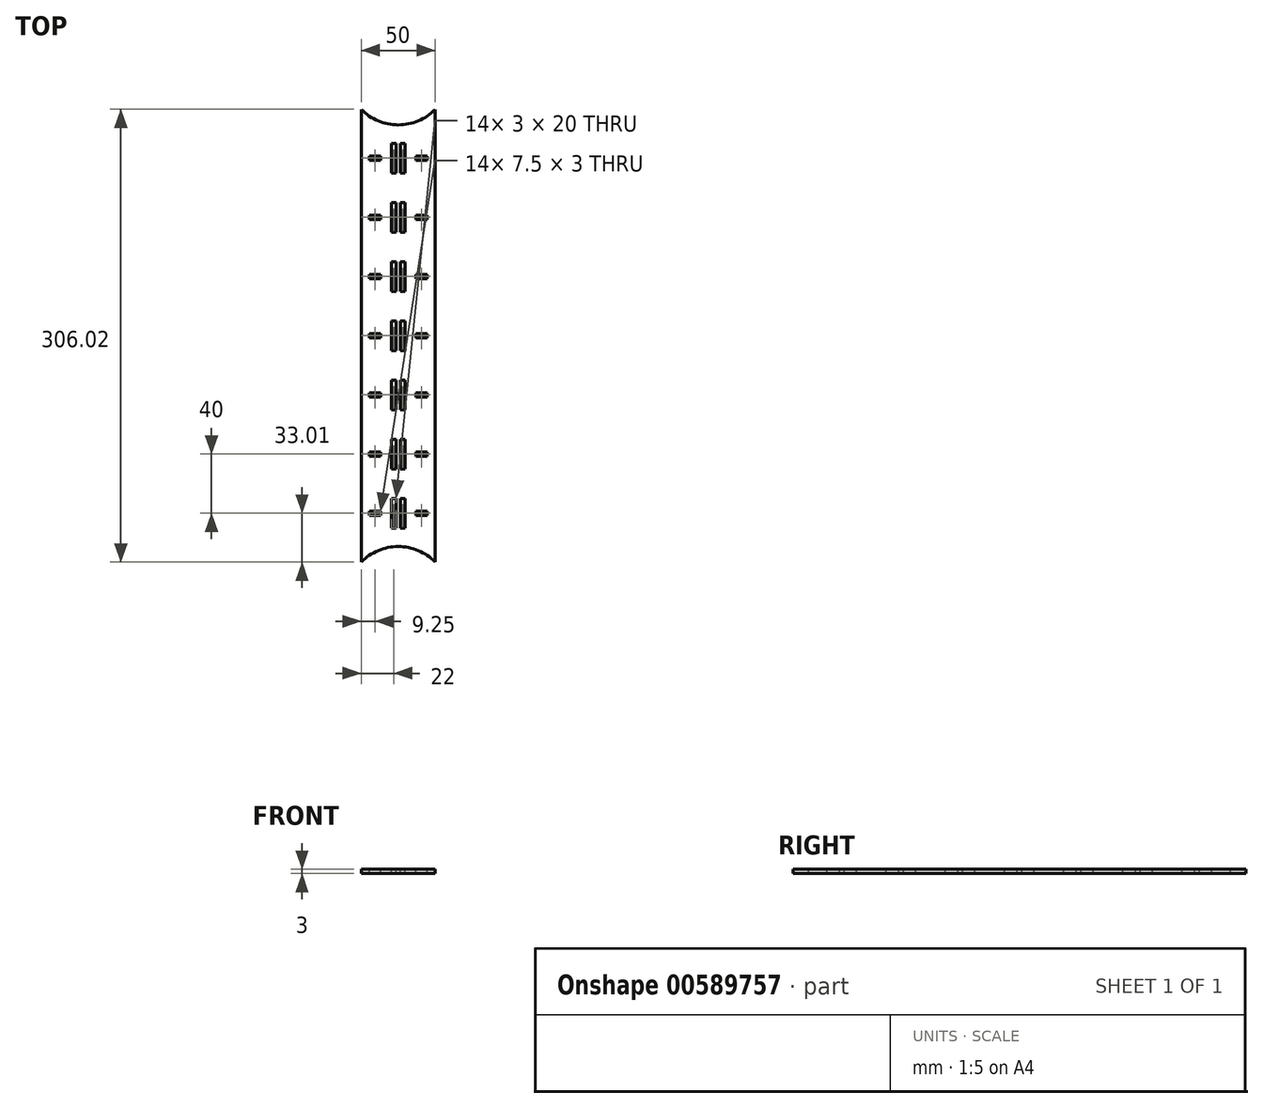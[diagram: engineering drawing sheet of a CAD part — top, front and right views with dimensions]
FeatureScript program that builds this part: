
annotation { "Feature Type Name" : "Feature", "Feature Type Description" : "" }
export const myFeature = defineFeature(function(context is Context, id is Id, definition is map)
    precondition{}
    {
        {
            var Q0;
            Q0=qCreatedBy(makeId("Top.planeOp"),FACE);
            var sketch = newSketch(context, id + "F0", { "sketchPlane" : qUnion([Q0])});
            skLineSegment(sketch, "E0.bottom", {"start": v(25, 140) * mm, "end": v(-25, 140) * mm});
            skLineSegment(sketch, "E0.top", {"start": v(25, -140) * mm, "end": v(-25, -140) * mm});
            skLineSegment(sketch, "E0.left", {"start": v(25, 140) * mm, "end": v(25, -140) * mm});
            skLineSegment(sketch, "E0.right", {"start": v(-25, 140) * mm, "end": v(-25, -140) * mm});
            skPoint(sketch, "E0.middle", {"position": v(0, 0) * mm});
            skSolve(sketch);
        }
        {
            var Q0;
            Q0=makeQuery(id+"F0.imprint","IMPRINT",FACE,{"disambiguationData":[TD([[makeQuery(id+"F0.imprint","IMPRINT",EDGE,{"derivedFrom":sQuery(id+"F0.wireOp",EDGE,"E0.bottom")}),1.0]])]});
            extrude(context, id + "F1", {"entities" : qUnion([Q0]), "depth" : 3 * mm, "offsetDistance" : 25 * mm});
        }
        {
            var Q0;
            Q0=makeQuery(id+"F1.opExtrude","CAP_FACE",FACE,{"disambiguationData":[OSD([sQuery(id+"F0.wireOp",EDGE,"E0.bottom"),sQuery(id+"F0.wireOp",EDGE,"E0.top"),sQuery(id+"F0.wireOp",EDGE,"E0.left"),sQuery(id+"F0.wireOp",EDGE,"E0.right")])],"isStart":false});
            var sketch = newSketch(context, id + "F2", { "sketchPlane" : qUnion([Q0])});
            skLineSegment(sketch, "E1", {"start": v(0, 140) * mm, "end": v(0, -140) * mm, "construction": true});
            skLineSegment(sketch, "E2.bottom", {"start": v(1.5, 140) * mm, "end": v(-1.5, 140) * mm, "construction": true});
            skLineSegment(sketch, "E2.top", {"start": v(1.5, -140) * mm, "end": v(-1.5, -140) * mm, "construction": true});
            skLineSegment(sketch, "E2.left", {"start": v(1.5, 140) * mm, "end": v(1.5, 130) * mm, "construction": true});
            skLineSegment(sketch, "E2.right", {"start": v(-1.5, 140) * mm, "end": v(-1.5, 130) * mm, "construction": true});
            skPoint(sketch, "E2.middle", {"position": v(0, 0) * mm});
            skLineSegment(sketch, "E3.bottom", {"start": v(1.5, 130) * mm, "end": v(4.5, 130) * mm});
            skLineSegment(sketch, "E3.top", {"start": v(1.5, 110) * mm, "end": v(4.5, 110) * mm});
            skLineSegment(sketch, "E3.right", {"start": v(4.5, 130) * mm, "end": v(4.5, 110) * mm});
            skLineSegment(sketch, "E4.trimOffspring", {"start": v(1.5, 110) * mm, "end": v(1.5, -140) * mm, "construction": true});
            skLineSegment(sketch, "E5", {"start": v(1.5, 130) * mm, "end": v(1.5, 110) * mm});
            skLineSegment(sketch, "E6.0.1.0", {"start": v(4.5, 90) * mm, "end": v(4.5, 70) * mm});
            skLineSegment(sketch, "E6.0.1.1", {"start": v(1.5, 90) * mm, "end": v(4.5, 90) * mm});
            skLineSegment(sketch, "E6.0.1.2", {"start": v(1.5, 90) * mm, "end": v(1.5, 70) * mm});
            skLineSegment(sketch, "E6.0.1.3", {"start": v(1.5, 70) * mm, "end": v(4.5, 70) * mm});
            skLineSegment(sketch, "E6.0.2.0", {"start": v(4.5, 50) * mm, "end": v(4.5, 30) * mm});
            skLineSegment(sketch, "E6.0.2.1", {"start": v(1.5, 50) * mm, "end": v(4.5, 50) * mm});
            skLineSegment(sketch, "E6.0.2.2", {"start": v(1.5, 50) * mm, "end": v(1.5, 30) * mm});
            skLineSegment(sketch, "E6.0.2.3", {"start": v(1.5, 30) * mm, "end": v(4.5, 30) * mm});
            skLineSegment(sketch, "E6.0.3.0", {"start": v(4.5, 10) * mm, "end": v(4.5, -10) * mm});
            skLineSegment(sketch, "E6.0.3.1", {"start": v(1.5, 10) * mm, "end": v(4.5, 10) * mm});
            skLineSegment(sketch, "E6.0.3.2", {"start": v(1.5, 10) * mm, "end": v(1.5, -10) * mm});
            skLineSegment(sketch, "E6.0.3.3", {"start": v(1.5, -10) * mm, "end": v(4.5, -10) * mm});
            skLineSegment(sketch, "E6.0.4.0", {"start": v(4.5, -30) * mm, "end": v(4.5, -50) * mm});
            skLineSegment(sketch, "E6.0.4.1", {"start": v(1.5, -30) * mm, "end": v(4.5, -30) * mm});
            skLineSegment(sketch, "E6.0.4.2", {"start": v(1.5, -30) * mm, "end": v(1.5, -50) * mm});
            skLineSegment(sketch, "E6.0.4.3", {"start": v(1.5, -50) * mm, "end": v(4.5, -50) * mm});
            skLineSegment(sketch, "E6.0.5.0", {"start": v(4.5, -70) * mm, "end": v(4.5, -90) * mm});
            skLineSegment(sketch, "E6.0.5.1", {"start": v(1.5, -70) * mm, "end": v(4.5, -70) * mm});
            skLineSegment(sketch, "E6.0.5.2", {"start": v(1.5, -70) * mm, "end": v(1.5, -90) * mm});
            skLineSegment(sketch, "E6.0.5.3", {"start": v(1.5, -90) * mm, "end": v(4.5, -90) * mm});
            skLineSegment(sketch, "E6.0.6.0", {"start": v(4.5, -110) * mm, "end": v(4.5, -130) * mm});
            skLineSegment(sketch, "E6.0.6.1", {"start": v(1.5, -110) * mm, "end": v(4.5, -110) * mm});
            skLineSegment(sketch, "E6.0.6.2", {"start": v(1.5, -110) * mm, "end": v(1.5, -130) * mm});
            skLineSegment(sketch, "E6.0.6.3", {"start": v(1.5, -130) * mm, "end": v(4.5, -130) * mm});
            skLineSegment(sketch, "E6.direction1", {"start": v(4.5, 110) * mm, "end": v(29.5, 110) * mm, "construction": true});
            skLineSegment(sketch, "E6.direction2", {"start": v(4.5, 110) * mm, "end": v(4.5, 70) * mm, "construction": true});
            skLineSegment(sketch, "E7.bottom", {"start": v(-1.5, 130) * mm, "end": v(-4.5, 130) * mm});
            skLineSegment(sketch, "E7.top", {"start": v(-1.5, 110) * mm, "end": v(-4.5, 110) * mm});
            skLineSegment(sketch, "E7.right", {"start": v(-4.5, 130) * mm, "end": v(-4.5, 110) * mm});
            skLineSegment(sketch, "E8.trimOffspring", {"start": v(-1.5, 110) * mm, "end": v(-1.5, -140) * mm, "construction": true});
            skLineSegment(sketch, "E9", {"start": v(-1.5, 130) * mm, "end": v(-1.5, 110) * mm});
            skLineSegment(sketch, "E10.0.1.0", {"start": v(-1.5, 90) * mm, "end": v(-4.5, 90) * mm});
            skLineSegment(sketch, "E10.0.1.1", {"start": v(-1.5, 90) * mm, "end": v(-1.5, 70) * mm});
            skLineSegment(sketch, "E10.0.1.2", {"start": v(-4.5, 90) * mm, "end": v(-4.5, 70) * mm});
            skLineSegment(sketch, "E10.0.1.3", {"start": v(-1.5, 70) * mm, "end": v(-4.5, 70) * mm});
            skLineSegment(sketch, "E10.0.2.0", {"start": v(-1.5, 50) * mm, "end": v(-4.5, 50) * mm});
            skLineSegment(sketch, "E10.0.2.1", {"start": v(-1.5, 50) * mm, "end": v(-1.5, 30) * mm});
            skLineSegment(sketch, "E10.0.2.2", {"start": v(-4.5, 50) * mm, "end": v(-4.5, 30) * mm});
            skLineSegment(sketch, "E10.0.2.3", {"start": v(-1.5, 30) * mm, "end": v(-4.5, 30) * mm});
            skLineSegment(sketch, "E10.0.3.0", {"start": v(-1.5, 10) * mm, "end": v(-4.5, 10) * mm});
            skLineSegment(sketch, "E10.0.3.1", {"start": v(-1.5, 10) * mm, "end": v(-1.5, -10) * mm});
            skLineSegment(sketch, "E10.0.3.2", {"start": v(-4.5, 10) * mm, "end": v(-4.5, -10) * mm});
            skLineSegment(sketch, "E10.0.3.3", {"start": v(-1.5, -10) * mm, "end": v(-4.5, -10) * mm});
            skLineSegment(sketch, "E10.0.4.0", {"start": v(-1.5, -30) * mm, "end": v(-4.5, -30) * mm});
            skLineSegment(sketch, "E10.0.4.1", {"start": v(-1.5, -30) * mm, "end": v(-1.5, -50) * mm});
            skLineSegment(sketch, "E10.0.4.2", {"start": v(-4.5, -30) * mm, "end": v(-4.5, -50) * mm});
            skLineSegment(sketch, "E10.0.4.3", {"start": v(-1.5, -50) * mm, "end": v(-4.5, -50) * mm});
            skLineSegment(sketch, "E10.0.5.0", {"start": v(-1.5, -70) * mm, "end": v(-4.5, -70) * mm});
            skLineSegment(sketch, "E10.0.5.1", {"start": v(-1.5, -70) * mm, "end": v(-1.5, -90) * mm});
            skLineSegment(sketch, "E10.0.5.2", {"start": v(-4.5, -70) * mm, "end": v(-4.5, -90) * mm});
            skLineSegment(sketch, "E10.0.5.3", {"start": v(-1.5, -90) * mm, "end": v(-4.5, -90) * mm});
            skLineSegment(sketch, "E10.0.6.0", {"start": v(-1.5, -110) * mm, "end": v(-4.5, -110) * mm});
            skLineSegment(sketch, "E10.0.6.1", {"start": v(-1.5, -110) * mm, "end": v(-1.5, -130) * mm});
            skLineSegment(sketch, "E10.0.6.2", {"start": v(-4.5, -110) * mm, "end": v(-4.5, -130) * mm});
            skLineSegment(sketch, "E10.0.6.3", {"start": v(-1.5, -130) * mm, "end": v(-4.5, -130) * mm});
            skLineSegment(sketch, "E10.direction1", {"start": v(-4.5, 130) * mm, "end": v(20.5, 130) * mm, "construction": true});
            skLineSegment(sketch, "E10.direction2", {"start": v(-4.5, 130) * mm, "end": v(-4.5, 90) * mm, "construction": true});
            skSolve(sketch);
        }
        {
            var Q0;
            Q0 = qSketchRegion(id + "F2", true);
            extrude(context, id + "F3", {"entities" : qUnion([Q0]), "operationType" : NewBodyOperationType.REMOVE, "oppositeDirection" : true, "depth" : 25 * mm, "offsetDistance" : 25 * mm});
        }
        {
            var Q0;
            Q0=makeQuery(id+"F1.opExtrude","CAP_FACE",FACE,{"disambiguationData":[OSD([sQuery(id+"F0.wireOp",EDGE,"E0.bottom"),sQuery(id+"F0.wireOp",EDGE,"E0.top"),sQuery(id+"F0.wireOp",EDGE,"E0.left"),sQuery(id+"F0.wireOp",EDGE,"E0.right")])],"isStart":false});
            var sketch = newSketch(context, id + "F4", { "sketchPlane" : qUnion([Q0])});
            skLineSegment(sketch, "E11", {"start": v(4.5, 120) * mm, "end": v(12, 120) * mm, "construction": true});
            skLineSegment(sketch, "E12", {"start": v(12, 120) * mm, "end": v(19.5, 120) * mm, "construction": true});
            skLineSegment(sketch, "E13.bottom", {"start": v(19.5, 121.5) * mm, "end": v(12, 121.5) * mm});
            skLineSegment(sketch, "E13.top", {"start": v(19.5, 118.5) * mm, "end": v(12, 118.5) * mm});
            skLineSegment(sketch, "E13.left", {"start": v(19.5, 121.5) * mm, "end": v(19.5, 118.5) * mm});
            skLineSegment(sketch, "E13.right", {"start": v(12, 121.5) * mm, "end": v(12, 118.5) * mm});
            skPoint(sketch, "E13.middle", {"position": v(15.75, 120) * mm});
            skLineSegment(sketch, "E14.0.1.0", {"start": v(19.5, 81.5) * mm, "end": v(12, 81.5) * mm});
            skLineSegment(sketch, "E14.0.1.1", {"start": v(12, 81.5) * mm, "end": v(12, 78.5) * mm});
            skLineSegment(sketch, "E14.0.1.2", {"start": v(19.5, 78.5) * mm, "end": v(12, 78.5) * mm});
            skLineSegment(sketch, "E14.0.1.3", {"start": v(19.5, 81.5) * mm, "end": v(19.5, 78.5) * mm});
            skLineSegment(sketch, "E14.0.2.0", {"start": v(19.5, 41.5) * mm, "end": v(12, 41.5) * mm});
            skLineSegment(sketch, "E14.0.2.1", {"start": v(12, 41.5) * mm, "end": v(12, 38.5) * mm});
            skLineSegment(sketch, "E14.0.2.2", {"start": v(19.5, 38.5) * mm, "end": v(12, 38.5) * mm});
            skLineSegment(sketch, "E14.0.2.3", {"start": v(19.5, 41.5) * mm, "end": v(19.5, 38.5) * mm});
            skLineSegment(sketch, "E14.0.3.0", {"start": v(19.5, 1.5) * mm, "end": v(12, 1.5) * mm});
            skLineSegment(sketch, "E14.0.3.1", {"start": v(12, 1.5) * mm, "end": v(12, -1.5) * mm});
            skLineSegment(sketch, "E14.0.3.2", {"start": v(19.5, -1.5) * mm, "end": v(12, -1.5) * mm});
            skLineSegment(sketch, "E14.0.3.3", {"start": v(19.5, 1.5) * mm, "end": v(19.5, -1.5) * mm});
            skLineSegment(sketch, "E14.0.4.0", {"start": v(19.5, -38.5) * mm, "end": v(12, -38.5) * mm});
            skLineSegment(sketch, "E14.0.4.1", {"start": v(12, -38.5) * mm, "end": v(12, -41.5) * mm});
            skLineSegment(sketch, "E14.0.4.2", {"start": v(19.5, -41.5) * mm, "end": v(12, -41.5) * mm});
            skLineSegment(sketch, "E14.0.4.3", {"start": v(19.5, -38.5) * mm, "end": v(19.5, -41.5) * mm});
            skLineSegment(sketch, "E14.0.5.0", {"start": v(19.5, -78.5) * mm, "end": v(12, -78.5) * mm});
            skLineSegment(sketch, "E14.0.5.1", {"start": v(12, -78.5) * mm, "end": v(12, -81.5) * mm});
            skLineSegment(sketch, "E14.0.5.2", {"start": v(19.5, -81.5) * mm, "end": v(12, -81.5) * mm});
            skLineSegment(sketch, "E14.0.5.3", {"start": v(19.5, -78.5) * mm, "end": v(19.5, -81.5) * mm});
            skLineSegment(sketch, "E14.0.6.0", {"start": v(19.5, -118.5) * mm, "end": v(12, -118.5) * mm});
            skLineSegment(sketch, "E14.0.6.1", {"start": v(12, -118.5) * mm, "end": v(12, -121.5) * mm});
            skLineSegment(sketch, "E14.0.6.2", {"start": v(19.5, -121.5) * mm, "end": v(12, -121.5) * mm});
            skLineSegment(sketch, "E14.0.6.3", {"start": v(19.5, -118.5) * mm, "end": v(19.5, -121.5) * mm});
            skLineSegment(sketch, "E14.direction1", {"start": v(12, 118.5) * mm, "end": v(37, 118.5) * mm, "construction": true});
            skLineSegment(sketch, "E14.direction2", {"start": v(12, 118.5) * mm, "end": v(12, 78.5) * mm, "construction": true});
            skLineSegment(sketch, "E15", {"start": v(0, 140) * mm, "end": v(0, 132.73) * mm, "construction": true});
            skPoint(sketch, "E15.endSnap0", {"position": v(0, 140) * mm});
            skLineSegment(sketch, "E16.MirrorCS", {"start": v(-19.5, 121.5) * mm, "end": v(-12, 121.5) * mm});
            skLineSegment(sketch, "E17.MirrorCS", {"start": v(-19.5, 118.5) * mm, "end": v(-12, 118.5) * mm});
            skLineSegment(sketch, "E18.MirrorCS", {"start": v(-12, 121.5) * mm, "end": v(-12, 118.5) * mm});
            skLineSegment(sketch, "E19.MirrorCS", {"start": v(-12, 120) * mm, "end": v(-19.5, 120) * mm, "construction": true});
            skLineSegment(sketch, "E20.MirrorCS", {"start": v(-19.5, 121.5) * mm, "end": v(-19.5, 118.5) * mm});
            skLineSegment(sketch, "E21.MirrorCS", {"start": v(-19.5, -78.5) * mm, "end": v(-19.5, -81.5) * mm});
            skLineSegment(sketch, "E22.MirrorCS", {"start": v(-19.5, 41.5) * mm, "end": v(-19.5, 38.5) * mm});
            skLineSegment(sketch, "E23.MirrorCS", {"start": v(-19.5, 81.5) * mm, "end": v(-12, 81.5) * mm});
            skLineSegment(sketch, "E24.MirrorCS", {"start": v(-12, 81.5) * mm, "end": v(-12, 78.5) * mm});
            skLineSegment(sketch, "E25.MirrorCS", {"start": v(-19.5, 78.5) * mm, "end": v(-12, 78.5) * mm});
            skLineSegment(sketch, "E26.MirrorCS", {"start": v(-19.5, -78.5) * mm, "end": v(-12, -78.5) * mm});
            skLineSegment(sketch, "E27.MirrorCS", {"start": v(-19.5, -38.5) * mm, "end": v(-12, -38.5) * mm});
            skLineSegment(sketch, "E28.MirrorCS", {"start": v(-19.5, -118.5) * mm, "end": v(-12, -118.5) * mm});
            skLineSegment(sketch, "E29.MirrorCS", {"start": v(-12, -38.5) * mm, "end": v(-12, -41.5) * mm});
            skLineSegment(sketch, "E30.MirrorCS", {"start": v(-19.5, -1.5) * mm, "end": v(-12, -1.5) * mm});
            skLineSegment(sketch, "E31.MirrorCS", {"start": v(-12, -118.5) * mm, "end": v(-12, -121.5) * mm});
            skLineSegment(sketch, "E32.MirrorCS", {"start": v(-19.5, -118.5) * mm, "end": v(-19.5, -121.5) * mm});
            skLineSegment(sketch, "E33.MirrorCS", {"start": v(-19.5, -41.5) * mm, "end": v(-12, -41.5) * mm});
            skLineSegment(sketch, "E34.MirrorCS", {"start": v(-19.5, 1.5) * mm, "end": v(-12, 1.5) * mm});
            skLineSegment(sketch, "E35.MirrorCS", {"start": v(-12, 1.5) * mm, "end": v(-12, -1.5) * mm});
            skLineSegment(sketch, "E36.MirrorCS", {"start": v(-12, -78.5) * mm, "end": v(-12, -81.5) * mm});
            skLineSegment(sketch, "E37.MirrorCS", {"start": v(-19.5, 81.5) * mm, "end": v(-19.5, 78.5) * mm});
            skLineSegment(sketch, "E38.MirrorCS", {"start": v(-19.5, 41.5) * mm, "end": v(-12, 41.5) * mm});
            skLineSegment(sketch, "E39.MirrorCS", {"start": v(-19.5, -121.5) * mm, "end": v(-12, -121.5) * mm});
            skLineSegment(sketch, "E40.MirrorCS", {"start": v(-12, 41.5) * mm, "end": v(-12, 38.5) * mm});
            skLineSegment(sketch, "E41.MirrorCS", {"start": v(-19.5, 38.5) * mm, "end": v(-12, 38.5) * mm});
            skLineSegment(sketch, "E42.MirrorCS", {"start": v(-19.5, -81.5) * mm, "end": v(-12, -81.5) * mm});
            skLineSegment(sketch, "E43.MirrorCS", {"start": v(-19.5, 1.5) * mm, "end": v(-19.5, -1.5) * mm});
            skLineSegment(sketch, "E44.MirrorCS", {"start": v(-19.5, -38.5) * mm, "end": v(-19.5, -41.5) * mm});
            skPoint(sketch, "E45.MirrorP", {"position": v(-15.75, 120) * mm});
            skLineSegment(sketch, "E46.MirrorCS", {"start": v(-12, 118.5) * mm, "end": v(-12, 78.5) * mm, "construction": true});
            skLineSegment(sketch, "E47.MirrorCS", {"start": v(-12, 118.5) * mm, "end": v(-37, 118.5) * mm, "construction": true});
            skSolve(sketch);
        }
        {
            var Q0;
            Q0 = qSketchRegion(id + "F4", true);
            extrude(context, id + "F5", {"entities" : qUnion([Q0]), "operationType" : NewBodyOperationType.REMOVE, "oppositeDirection" : true, "depth" : 25 * mm, "offsetDistance" : 25 * mm});
        }
        {
            var Q0;
            Q0=makeQuery(id+"F1.opExtrude","CAP_FACE",FACE,{"disambiguationData":[OSD([sQuery(id+"F0.wireOp",EDGE,"E0.bottom"),sQuery(id+"F0.wireOp",EDGE,"E0.top"),sQuery(id+"F0.wireOp",EDGE,"E0.left"),sQuery(id+"F0.wireOp",EDGE,"E0.right")])],"isStart":false});
            var sketch = newSketch(context, id + "F6", { "sketchPlane" : qUnion([Q0])});
            skLineSegment(sketch, "E48", {"start": v(0, 140) * mm, "end": v(0, 142.5) * mm, "construction": true});
            skPoint(sketch, "E48.endSnap0", {"position": v(0, 140) * mm});
            skLineSegment(sketch, "E49", {"start": v(0, 142.5) * mm, "end": v(0, 177.5) * mm, "construction": true});
            skArc(sketch, "E50", {"start": v(-25, 153) * mm, "mid": v(0, 142.5) * mm, "end": v(25, 153) * mm});
            skLineSegment(sketch, "E51", {"start": v(-25, 140) * mm, "end": v(-25, 153) * mm});
            skLineSegment(sketch, "E52.MirrorCS", {"start": v(25, 140) * mm, "end": v(25, 153) * mm});
            skLineSegment(sketch, "E53", {"start": v(-25, 140) * mm, "end": v(25, 140) * mm});
            skLineSegment(sketch, "E54.MirrorCS", {"start": v(0, -140) * mm, "end": v(0, -142.5) * mm, "construction": true});
            skPoint(sketch, "E55.MirrorP", {"position": v(0, -140) * mm});
            skLineSegment(sketch, "E56.MirrorCS", {"start": v(-25, -140) * mm, "end": v(25, -140) * mm});
            skLineSegment(sketch, "E57.MirrorCS", {"start": v(25, -140) * mm, "end": v(25, -153) * mm});
            skLineSegment(sketch, "E58.MirrorCS", {"start": v(-25, -140) * mm, "end": v(-25, -153) * mm});
            skArc(sketch, "E59.MirrorCS", {"start": v(-25, -153) * mm, "mid": v(0, -142.5) * mm, "end": v(25, -153) * mm});
            skSolve(sketch);
        }
        {
            var Q0;
            Q0 = qSketchRegion(id + "F6", true);
            extrude(context, id + "F7", {"entities" : qUnion([Q0]), "operationType" : NewBodyOperationType.ADD, "oppositeDirection" : true, "depth" : 3 * mm, "offsetDistance" : 25 * mm});
        }
    });
